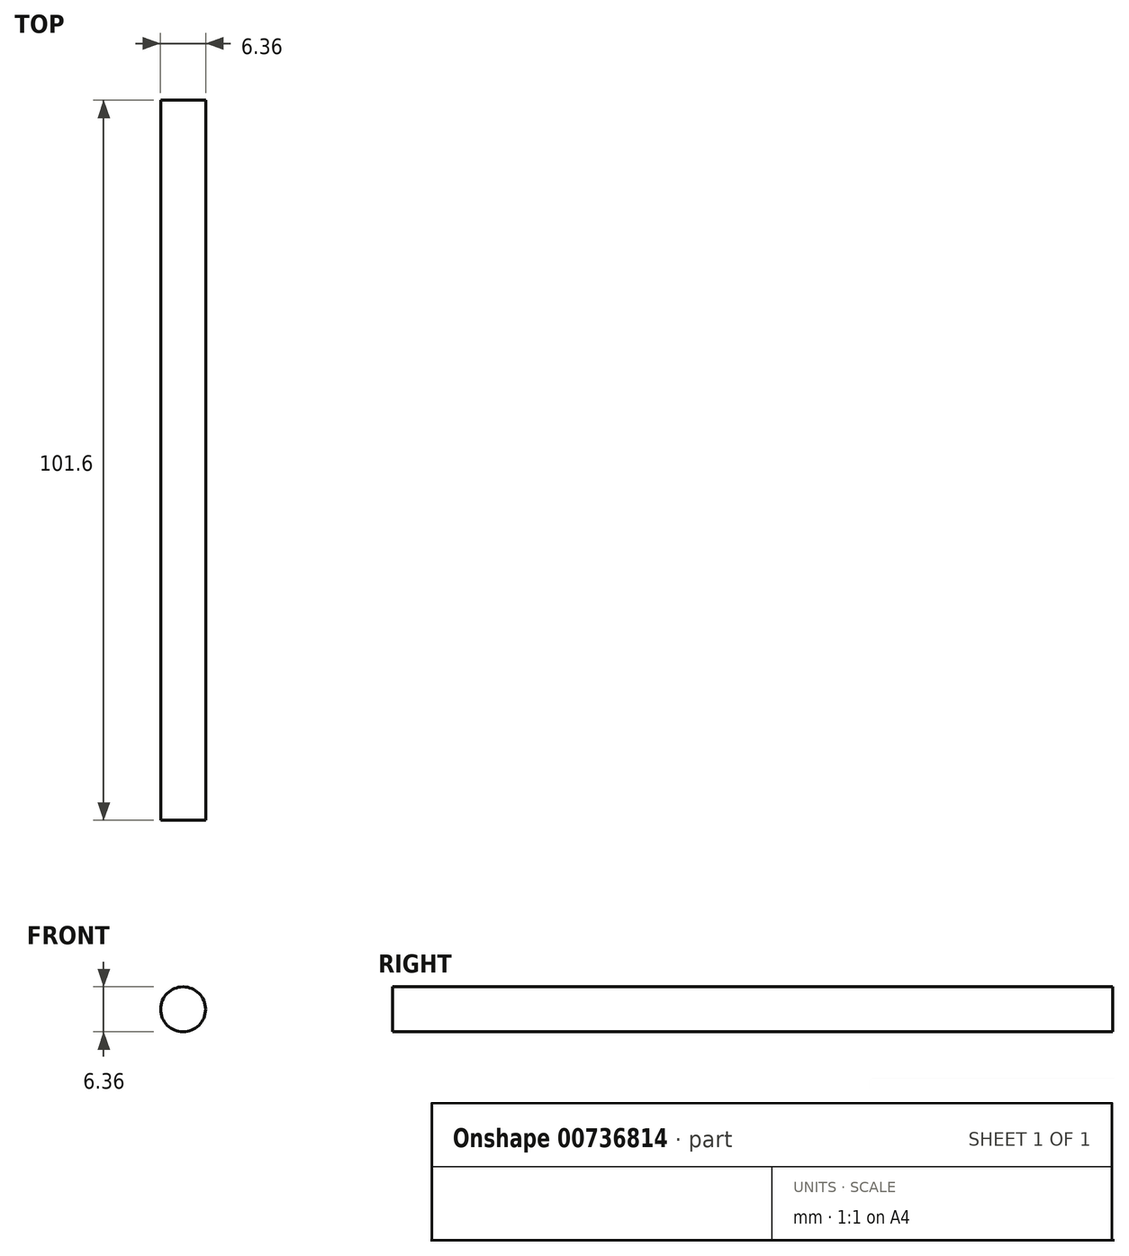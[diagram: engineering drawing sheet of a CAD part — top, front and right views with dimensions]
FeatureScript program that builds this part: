
annotation { "Feature Type Name" : "Feature", "Feature Type Description" : "" }
export const myFeature = defineFeature(function(context is Context, id is Id, definition is map)
    precondition{}
    {
        {
            var Q0;
            Q0=qCreatedBy(makeId("Front.planeOp"),FACE);
            var sketch = newSketch(context, id + "F0", { "sketchPlane" : qUnion([Q0])});
            skCircle(sketch, "E0", {"center": v(0, 0) * mm, "radius": 3.18 * mm});
            skSolve(sketch);
        }
        {
            var Q0;
            Q0=makeQuery(id+"F0.imprint","IMPRINT",FACE,{"disambiguationData":[TD([[makeQuery(id+"F0.imprint","IMPRINT",EDGE,{"derivedFrom":sQuery(id+"F0.wireOp",EDGE,"E0")}),1.0]])]});
            extrude(context, id + "F1", {"entities" : qUnion([Q0]), "depth" : 101.6 * mm, "offsetDistance" : 25.4 * mm});
        }
    });
